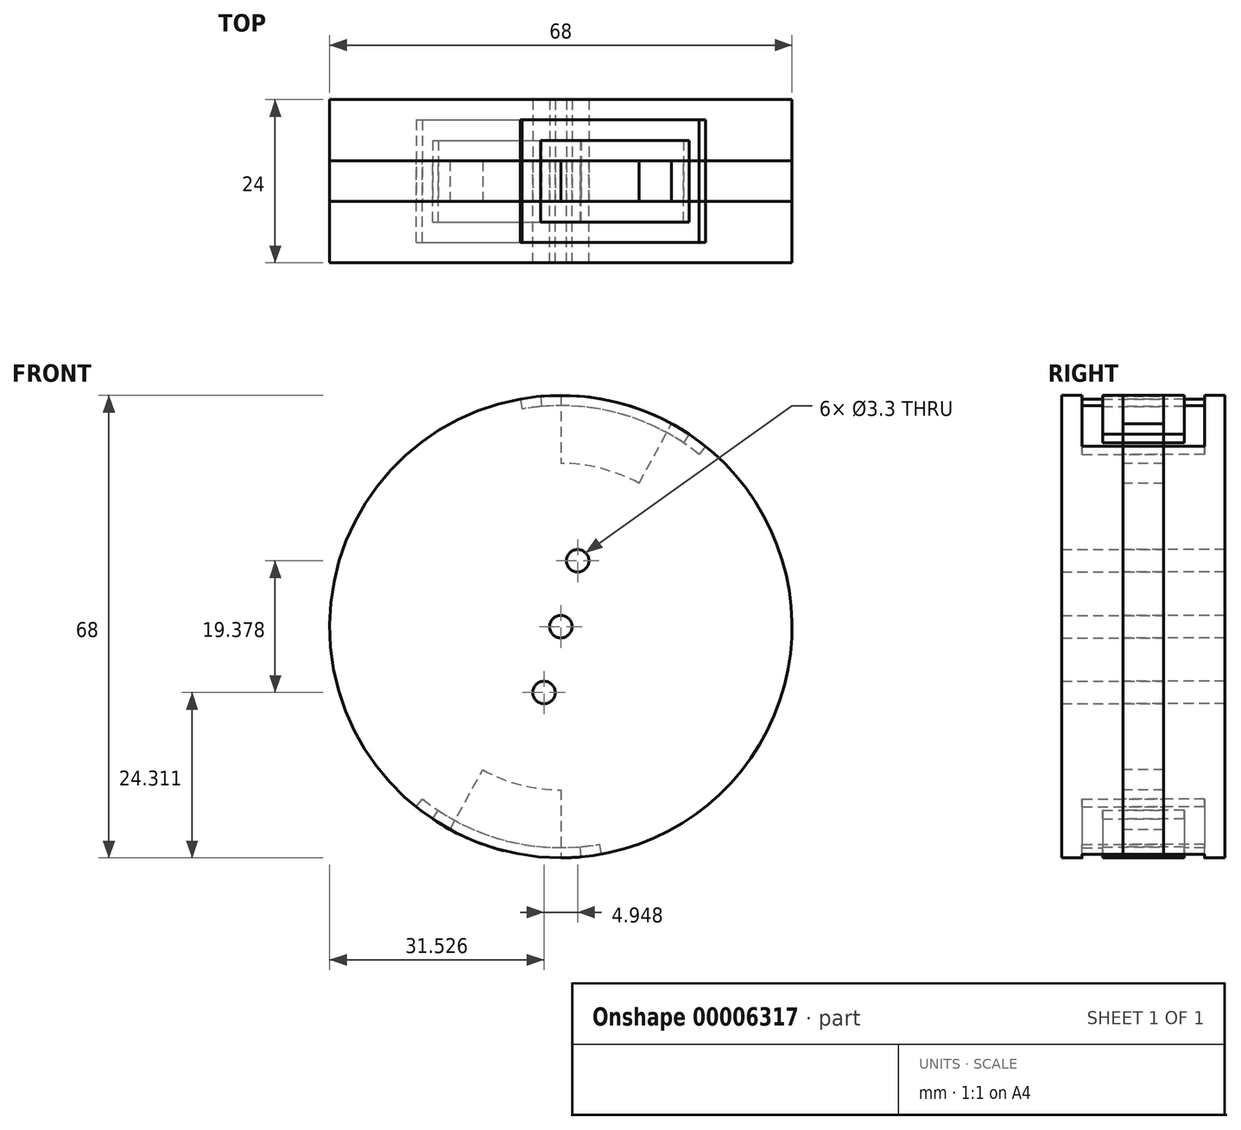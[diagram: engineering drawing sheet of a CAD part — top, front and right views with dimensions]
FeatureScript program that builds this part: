
annotation { "Feature Type Name" : "Feature", "Feature Type Description" : "" }
export const myFeature = defineFeature(function(context is Context, id is Id, definition is map)
    precondition{}
    {
        {
            var Q0;
            Q0=qCreatedBy(makeId("Front.planeOp"),FACE);
            var sketch = newSketch(context, id + "F0", { "sketchPlane" : qUnion([Q0])});
            skArc(sketch, "E0", {"start": v(0, 34) * mm, "mid": v(-1.5, 33.97) * mm, "end": v(-3, 33.87) * mm});
            skLineSegment(sketch, "E1", {"start": v(0, 34) * mm, "end": v(0, 24) * mm});
            skArc(sketch, "E2", {"start": v(11.5, 21.06) * mm, "mid": v(5.94, 23.25) * mm, "end": v(0, 24) * mm});
            skLineSegment(sketch, "E3", {"start": v(11.5, 21.06) * mm, "end": v(16.3, 29.84) * mm});
            skLineSegment(sketch, "E4", {"start": v(-5.97, 33.47) * mm, "end": v(-5.71, 32) * mm});
            skLineSegment(sketch, "E5", {"start": v(-3, 33.87) * mm, "end": v(-2.87, 32.37) * mm});
            skPoint(sketch, "E6", {"position": v(5.94, 23.25) * mm});
            skLineSegment(sketch, "E7", {"start": v(0, 0) * mm, "end": v(5.94, 23.25) * mm, "construction": true});
            skArc(sketch, "E8", {"start": v(-2.87, 32.37) * mm, "mid": v(-4.3, 32.22) * mm, "end": v(-5.71, 32) * mm});
            skLineSegment(sketch, "E9.0.MirrorCS", {"start": v(21.29, 26.5) * mm, "end": v(20.35, 25.34) * mm});
            skLineSegment(sketch, "E9.1.MirrorCS", {"start": v(18.87, 28.28) * mm, "end": v(18.04, 27.04) * mm});
            skArc(sketch, "E9.2.MirrorCS", {"start": v(18.04, 27.04) * mm, "mid": v(19.21, 26.21) * mm, "end": v(20.35, 25.34) * mm});
            skArc(sketch, "E10.trimOffspring", {"start": v(-5.97, 33.47) * mm, "mid": v(-32.94, 8.41) * mm, "end": v(-21.29, -26.5) * mm});
            skArc(sketch, "E11.trimOffspring", {"start": v(18.87, 28.28) * mm, "mid": v(17.6, 29.09) * mm, "end": v(16.3, 29.84) * mm});
            skArc(sketch, "E12", {"start": v(16.3, 29.84) * mm, "mid": v(8.41, 32.94) * mm, "end": v(0, 34) * mm, "construction": true});
            skCircle(sketch, "E13", {"center": v(0, 0) * mm, "radius": 1.65 * mm});
            skCircle(sketch, "E14", {"center": v(2.47, 9.69) * mm, "radius": 1.65 * mm});
            skLineSegment(sketch, "E15", {"start": v(0, 0) * mm, "end": v(32.94, -8.41) * mm, "construction": true});
            skLineSegment(sketch, "E16.0.MirrorCS", {"start": v(-21.29, -26.5) * mm, "end": v(-20.35, -25.34) * mm});
            skArc(sketch, "E17.0.MirrorCS", {"start": v(-18.04, -27.04) * mm, "mid": v(-19.21, -26.21) * mm, "end": v(-20.35, -25.34) * mm});
            skLineSegment(sketch, "E18.0.MirrorCS", {"start": v(-18.87, -28.28) * mm, "end": v(-18.04, -27.04) * mm});
            skLineSegment(sketch, "E19.0.MirrorCS", {"start": v(-16.3, -29.84) * mm, "end": v(-11.5, -21.06) * mm});
            skArc(sketch, "E20.0.MirrorCS", {"start": v(0, -24) * mm, "mid": v(-5.94, -23.25) * mm, "end": v(-11.5, -21.06) * mm});
            skLineSegment(sketch, "E21.0.MirrorCS", {"start": v(0, -24) * mm, "end": v(0, -34) * mm});
            skLineSegment(sketch, "E22.0.MirrorCS", {"start": v(3, -33.87) * mm, "end": v(2.87, -32.37) * mm});
            skArc(sketch, "E23.0.MirrorCS", {"start": v(2.87, -32.37) * mm, "mid": v(4.3, -32.22) * mm, "end": v(5.71, -32) * mm});
            skLineSegment(sketch, "E24.0.MirrorCS", {"start": v(5.97, -33.47) * mm, "end": v(5.71, -32) * mm});
            skArc(sketch, "E25.trimOffspring", {"start": v(-18.87, -28.28) * mm, "mid": v(-17.6, -29.09) * mm, "end": v(-16.3, -29.84) * mm});
            skArc(sketch, "E26.trimOffspring", {"start": v(0, -34) * mm, "mid": v(1.5, -33.97) * mm, "end": v(3, -33.87) * mm});
            skArc(sketch, "E27.trimOffspring", {"start": v(5.97, -33.47) * mm, "mid": v(32.94, -8.41) * mm, "end": v(21.29, 26.5) * mm});
            skCircle(sketch, "E28.0.MirrorC", {"center": v(-2.47, -9.69) * mm, "radius": 1.65 * mm});
            skSolve(sketch);
        }
        {
            var Q0;
            Q0=makeQuery(id+"F0.imprint","IMPRINT",FACE,{"disambiguationData":[TD([[makeQuery(id+"F0.imprint","IMPRINT",EDGE,{"derivedFrom":sQuery(id+"F0.wireOp",EDGE,"E0")}),1.0]])]});
            extrude(context, id + "F1", {"entities" : qUnion([Q0]), "endBound" : BoundingType.SYMMETRIC, "depth" : 6 * mm});
        }
        {
            var Q0;
            Q0=makeQuery(id+"F1.opExtrude","CAP_FACE",FACE,{"disambiguationData":[OSD([sQuery(id+"F0.wireOp",EDGE,"E0"),sQuery(id+"F0.wireOp",EDGE,"E1"),sQuery(id+"F0.wireOp",EDGE,"E2"),sQuery(id+"F0.wireOp",EDGE,"E3"),sQuery(id+"F0.wireOp",EDGE,"E4"),sQuery(id+"F0.wireOp",EDGE,"E5"),sQuery(id+"F0.wireOp",EDGE,"E8"),sQuery(id+"F0.wireOp",EDGE,"E9.0.MirrorCS"),sQuery(id+"F0.wireOp",EDGE,"E9.1.MirrorCS"),sQuery(id+"F0.wireOp",EDGE,"E9.2.MirrorCS"),sQuery(id+"F0.wireOp",EDGE,"E10.trimOffspring"),sQuery(id+"F0.wireOp",EDGE,"E11.trimOffspring")])],"isStart":false});
            var sketch = newSketch(context, id + "F2", { "sketchPlane" : qUnion([Q0])});
            skArc(sketch, "E29", {"start": v(-5.97, 33.47) * mm, "mid": v(-32.94, 8.41) * mm, "end": v(-21.29, -26.5) * mm});
            skLineSegment(sketch, "E30.0", {"start": v(-5.97, 33.47) * mm, "end": v(-5.71, 32) * mm});
            skArc(sketch, "E30.1", {"start": v(-2.87, 32.37) * mm, "mid": v(-4.3, 32.22) * mm, "end": v(-5.71, 32) * mm});
            skLineSegment(sketch, "E30.2", {"start": v(-3, 33.87) * mm, "end": v(-2.87, 32.37) * mm});
            skLineSegment(sketch, "E31.0", {"start": v(21.29, 26.5) * mm, "end": v(20.35, 25.34) * mm});
            skArc(sketch, "E31.1", {"start": v(18.04, 27.04) * mm, "mid": v(19.21, 26.21) * mm, "end": v(20.35, 25.34) * mm});
            skLineSegment(sketch, "E31.2", {"start": v(18.87, 28.28) * mm, "end": v(18.04, 27.04) * mm});
            skArc(sketch, "E32.trimOffspring", {"start": v(18.87, 28.28) * mm, "mid": v(8.41, 32.94) * mm, "end": v(-3, 33.87) * mm});
            skLineSegment(sketch, "E33.0", {"start": v(-21.29, -26.5) * mm, "end": v(-20.35, -25.34) * mm});
            skArc(sketch, "E33.1", {"start": v(-18.04, -27.04) * mm, "mid": v(-19.21, -26.21) * mm, "end": v(-20.35, -25.34) * mm});
            skLineSegment(sketch, "E33.2", {"start": v(-18.87, -28.28) * mm, "end": v(-18.04, -27.04) * mm});
            skLineSegment(sketch, "E33.3", {"start": v(3, -33.87) * mm, "end": v(2.87, -32.37) * mm});
            skArc(sketch, "E33.4", {"start": v(2.87, -32.37) * mm, "mid": v(4.3, -32.22) * mm, "end": v(5.71, -32) * mm});
            skLineSegment(sketch, "E33.5", {"start": v(5.97, -33.47) * mm, "end": v(5.71, -32) * mm});
            skArc(sketch, "E34.trimOffspring", {"start": v(-18.87, -28.28) * mm, "mid": v(-8.41, -32.94) * mm, "end": v(3, -33.87) * mm});
            skArc(sketch, "E35.trimOffspring", {"start": v(5.97, -33.47) * mm, "mid": v(32.94, -8.41) * mm, "end": v(21.29, 26.5) * mm});
            skCircle(sketch, "E36.0", {"center": v(0, 0) * mm, "radius": 1.65 * mm});
            skCircle(sketch, "E36.1", {"center": v(-2.47, -9.69) * mm, "radius": 1.65 * mm});
            skCircle(sketch, "E36.2", {"center": v(2.47, 9.69) * mm, "radius": 1.65 * mm});
            skSolve(sketch);
        }
        {
            var Q0;
            {var subQ5=makeQuery(id+"F1.opExtrude","CAP_EDGE",EDGE,{"disambiguationData":[OSD([sQuery(id+"F0.wireOp",EDGE,"E1")])],"isStart":false});Q0=makeQuery(id+"F2.imprint","IMPRINT",FACE,{"disambiguationData":[TD([[makeQuery(id+"F2.imprint","IMPRINT",EDGE,{"derivedFrom":subQ5}),-1.0]])]});}
            var Q1;
            {var subQ1=makeQuery(id+"F1.opExtrude","CAP_EDGE",EDGE,{"disambiguationData":[OSD([sQuery(id+"F0.wireOp",EDGE,"E1")])],"isStart":false});Q1=makeQuery(id+"F2.imprint","IMPRINT",FACE,{"disambiguationData":[TD([[makeQuery(id+"F2.imprint","IMPRINT",EDGE,{"derivedFrom":subQ1}),1.0]])]});}
            var Q2;
            {var subQ1=makeQuery(id+"F1.opExtrude","CAP_EDGE",EDGE,{"disambiguationData":[OSD([sQuery(id+"F0.wireOp",EDGE,"E19.0.MirrorCS")])],"isStart":false});Q2=makeQuery(id+"F2.imprint","IMPRINT",FACE,{"disambiguationData":[TD([[makeQuery(id+"F2.imprint","IMPRINT",EDGE,{"derivedFrom":subQ1}),-1.0]])]});}
            extrude(context, id + "F3", {"entities" : qUnion([Q0, Q1, Q2]), "operationType" : NewBodyOperationType.ADD, "depth" : 3 * mm});
        }
        {
            var Q0;
            Q0=makeQuery(id+"F3.opExtrude","CAP_FACE",FACE,{"disambiguationData":[OSD([sQuery(id+"F0.wireOp",EDGE,"E4"),sQuery(id+"F0.wireOp",EDGE,"E5"),sQuery(id+"F0.wireOp",EDGE,"E8"),sQuery(id+"F0.wireOp",EDGE,"E9.0.MirrorCS"),sQuery(id+"F0.wireOp",EDGE,"E9.1.MirrorCS"),sQuery(id+"F0.wireOp",EDGE,"E9.2.MirrorCS"),sQuery(id+"F2.wireOp",EDGE,"E29")])],"isStart":false});
            var sketch = newSketch(context, id + "F4", { "sketchPlane" : qUnion([Q0])});
            skArc(sketch, "E37", {"start": v(-20.35, -25.34) * mm, "mid": v(-8.04, -31.49) * mm, "end": v(5.71, -32) * mm});
            skArc(sketch, "E38.0", {"start": v(-5.97, 33.47) * mm, "mid": v(-32.94, 8.41) * mm, "end": v(-21.29, -26.5) * mm});
            skArc(sketch, "E38.1", {"start": v(5.97, -33.47) * mm, "mid": v(32.94, -8.41) * mm, "end": v(21.29, 26.5) * mm});
            skLineSegment(sketch, "E38.2", {"start": v(-5.97, 33.47) * mm, "end": v(-5.71, 32) * mm});
            skLineSegment(sketch, "E38.3", {"start": v(21.29, 26.5) * mm, "end": v(20.35, 25.34) * mm});
            skLineSegment(sketch, "E38.4", {"start": v(5.97, -33.47) * mm, "end": v(5.71, -32) * mm});
            skLineSegment(sketch, "E38.5", {"start": v(-21.29, -26.5) * mm, "end": v(-20.35, -25.34) * mm});
            skCircle(sketch, "E39.0", {"center": v(2.47, 9.69) * mm, "radius": 1.65 * mm});
            skCircle(sketch, "E39.1", {"center": v(0, 0) * mm, "radius": 1.65 * mm});
            skCircle(sketch, "E39.2", {"center": v(-2.47, -9.69) * mm, "radius": 1.65 * mm});
            skArc(sketch, "E40.trimOffspring", {"start": v(20.35, 25.34) * mm, "mid": v(8.04, 31.49) * mm, "end": v(-5.71, 32) * mm});
            skSolve(sketch);
        }
        {
            var Q0;
            {var subQ0=sQuery(id+"F4.wireOp",EDGE,"E37");var subQ2=makeQuery(id+"F4.imprint","INTERSECT",VERTEX,{"derivedFrom":[makeQuery(id+"F3.opExtrude","CAP_EDGE",EDGE,{"disambiguationData":[OSD([sQuery(id+"F0.wireOp",EDGE,"E4")])],"isStart":false}),subQ0]});var subQ4=makeQuery(id+"F4.imprint","INTERSECT",VERTEX,{"derivedFrom":[makeQuery(id+"F3.opExtrude","CAP_EDGE",EDGE,{"disambiguationData":[OSD([sQuery(id+"F0.wireOp",EDGE,"E5")])],"isStart":false}),subQ0]});Q0=makeQuery(id+"F4.imprint","IMPRINT",FACE,{"disambiguationData":[TD([[makeQuery(id+"F4.imprint","IMPRINT",EDGE,{"disambiguationData":[TD([[subQ2,1.0],[subQ4,-1.0]])],"derivedFrom":subQ0}),1.0]])]});}
            var Q1;
            {var subQ1=makeQuery(id+"F3.opExtrude","CAP_EDGE",EDGE,{"disambiguationData":[OSD([sQuery(id+"F0.wireOp",EDGE,"E4")])],"isStart":false});Q1=makeQuery(id+"F4.imprint","IMPRINT",FACE,{"disambiguationData":[TD([[makeQuery(id+"F4.imprint","IMPRINT",EDGE,{"derivedFrom":subQ1}),-1.0]])]});}
            var Q2;
            {var subQ1=makeQuery(id+"F3.opExtrude","CAP_EDGE",EDGE,{"disambiguationData":[OSD([sQuery(id+"F0.wireOp",EDGE,"E9.0.MirrorCS")])],"isStart":false});Q2=makeQuery(id+"F4.imprint","IMPRINT",FACE,{"disambiguationData":[TD([[makeQuery(id+"F4.imprint","IMPRINT",EDGE,{"derivedFrom":subQ1}),1.0]])]});}
            extrude(context, id + "F5", {"entities" : qUnion([Q0, Q1, Q2]), "operationType" : NewBodyOperationType.ADD, "depth" : 3 * mm});
        }
        {
            var Q0;
            Q0=makeQuery(id+"F5.opExtrude","CAP_FACE",FACE,{"disambiguationData":[OSD([sQuery(id+"F0.wireOp",EDGE,"E4"),sQuery(id+"F0.wireOp",EDGE,"E9.0.MirrorCS"),sQuery(id+"F4.wireOp",EDGE,"b19ecda2-b5bb-4668-8a59-7073f48bdfec"),sQuery(id+"F4.wireOp",EDGE,"E37")])],"isStart":false});
            var sketch = newSketch(context, id + "F6", { "sketchPlane" : qUnion([Q0])});
            skCircle(sketch, "E41", {"center": v(0, 0) * mm, "radius": 34 * mm});
            skCircle(sketch, "E42.0", {"center": v(2.47, 9.69) * mm, "radius": 1.65 * mm});
            skCircle(sketch, "E42.1", {"center": v(0, 0) * mm, "radius": 1.65 * mm});
            skCircle(sketch, "E42.2", {"center": v(-2.47, -9.69) * mm, "radius": 1.65 * mm});
            skSolve(sketch);
        }
        {
            var Q0;
            Q0=makeQuery(id+"F6.imprint","IMPRINT",FACE,{"disambiguationData":[TD([[makeQuery(id+"F6.imprint","IMPRINT",EDGE,{"derivedFrom":makeQuery(id+"F5.opExtrude","CAP_EDGE",EDGE,{"disambiguationData":[OSD([sQuery(id+"F4.wireOp",EDGE,"E37")])],"isStart":false})}),-1.0]])]});
            var Q1;
            Q1=makeQuery(id+"F6.imprint","IMPRINT",FACE,{"disambiguationData":[TD([[makeQuery(id+"F6.imprint","IMPRINT",EDGE,{"derivedFrom":makeQuery(id+"F5.opExtrude","CAP_EDGE",EDGE,{"disambiguationData":[OSD([sQuery(id+"F4.wireOp",EDGE,"E37")])],"isStart":false})}),1.0]])]});
            var Q2;
            {var subQ2=sQuery(id+"F0.wireOp",EDGE,"E4");var subQ3=makeQuery(id+"F5.opExtrude","CAP_EDGE",EDGE,{"disambiguationData":[OSD([subQ2])],"isStart":false});Q2=makeQuery(id+"F6.imprint","IMPRINT",FACE,{"disambiguationData":[TD([[makeQuery(id+"F6.imprint","IMPRINT",EDGE,{"derivedFrom":subQ3}),1.0]])]});}
            var Q3;
            {var subQ2=sQuery(id+"F0.wireOp",EDGE,"E9.0.MirrorCS");var subQ3=makeQuery(id+"F5.opExtrude","CAP_EDGE",EDGE,{"disambiguationData":[OSD([subQ2])],"isStart":false});Q3=makeQuery(id+"F6.imprint","IMPRINT",FACE,{"disambiguationData":[TD([[makeQuery(id+"F6.imprint","IMPRINT",EDGE,{"derivedFrom":subQ3}),-1.0]])]});}
            var Q4;
            {var subQ0=sQuery(id+"F0.wireOp",EDGE,"E22.0.MirrorCS");var subQ1=makeQuery(id+"F5.opExtrude","CAP_EDGE",EDGE,{"disambiguationData":[OSD([subQ0])],"isStart":false});Q4=makeQuery(id+"F6.imprint","IMPRINT",FACE,{"disambiguationData":[TD([[makeQuery(id+"F6.imprint","IMPRINT",EDGE,{"derivedFrom":subQ1}),-1.0]])]});}
            var Q5;
            {var subQ2=sQuery(id+"F0.wireOp",EDGE,"E16.0.MirrorCS");var subQ3=makeQuery(id+"F5.opExtrude","CAP_EDGE",EDGE,{"disambiguationData":[OSD([subQ2])],"isStart":false});Q5=makeQuery(id+"F6.imprint","IMPRINT",FACE,{"disambiguationData":[TD([[makeQuery(id+"F6.imprint","IMPRINT",EDGE,{"derivedFrom":subQ3}),-1.0]])]});}
            var Q6;
            {var subQ1=makeQuery(id+"F5.opExtrude","CAP_EDGE",EDGE,{"disambiguationData":[OSD([sQuery(id+"F4.wireOp",EDGE,"E38.2")])],"isStart":false});Q6=makeQuery(id+"F6.imprint","IMPRINT",FACE,{"disambiguationData":[TD([[makeQuery(id+"F6.imprint","IMPRINT",EDGE,{"derivedFrom":subQ1}),1.0]])]});}
            extrude(context, id + "F7", {"entities" : qUnion([Q0, Q1, Q2, Q3, Q4, Q5, Q6]), "operationType" : NewBodyOperationType.ADD, "depth" : 3 * mm});
        }
        {
            var Q0;
            Q0=makeQuery(id+"F1.opExtrude","SWEPT_BODY",BODY,{"disambiguationData":[OSD([sQuery(id+"F0.wireOp",EDGE,"E0"),sQuery(id+"F0.wireOp",EDGE,"E1"),sQuery(id+"F0.wireOp",EDGE,"E2"),sQuery(id+"F0.wireOp",EDGE,"E3"),sQuery(id+"F0.wireOp",EDGE,"E4"),sQuery(id+"F0.wireOp",EDGE,"E5"),sQuery(id+"F0.wireOp",EDGE,"E8"),sQuery(id+"F0.wireOp",EDGE,"E9.0.MirrorCS"),sQuery(id+"F0.wireOp",EDGE,"E9.1.MirrorCS"),sQuery(id+"F0.wireOp",EDGE,"E9.2.MirrorCS"),sQuery(id+"F0.wireOp",EDGE,"E10.trimOffspring"),sQuery(id+"F0.wireOp",EDGE,"E11.trimOffspring"),sQuery(id+"F0.wireOp",EDGE,"E13"),sQuery(id+"F0.wireOp",EDGE,"E14"),sQuery(id+"F0.wireOp",EDGE,"E16.0.MirrorCS"),sQuery(id+"F0.wireOp",EDGE,"E17.0.MirrorCS"),sQuery(id+"F0.wireOp",EDGE,"E18.0.MirrorCS"),sQuery(id+"F0.wireOp",EDGE,"E19.0.MirrorCS"),sQuery(id+"F0.wireOp",EDGE,"E20.0.MirrorCS"),sQuery(id+"F0.wireOp",EDGE,"E21.0.MirrorCS"),sQuery(id+"F0.wireOp",EDGE,"E22.0.MirrorCS"),sQuery(id+"F0.wireOp",EDGE,"E23.0.MirrorCS"),sQuery(id+"F0.wireOp",EDGE,"E24.0.MirrorCS"),sQuery(id+"F0.wireOp",EDGE,"E25.trimOffspring"),sQuery(id+"F0.wireOp",EDGE,"E26.trimOffspring"),sQuery(id+"F0.wireOp",EDGE,"E27.trimOffspring"),sQuery(id+"F0.wireOp",EDGE,"E28.0.MirrorC")])]});
            var Q1;
            Q1=qCreatedBy(makeId("Front.planeOp"),FACE);
            mirror(context, id + "F8", {"entities" : qUnion([Q0]), "mirrorPlane" : qUnion([Q1])});
        }
    });
